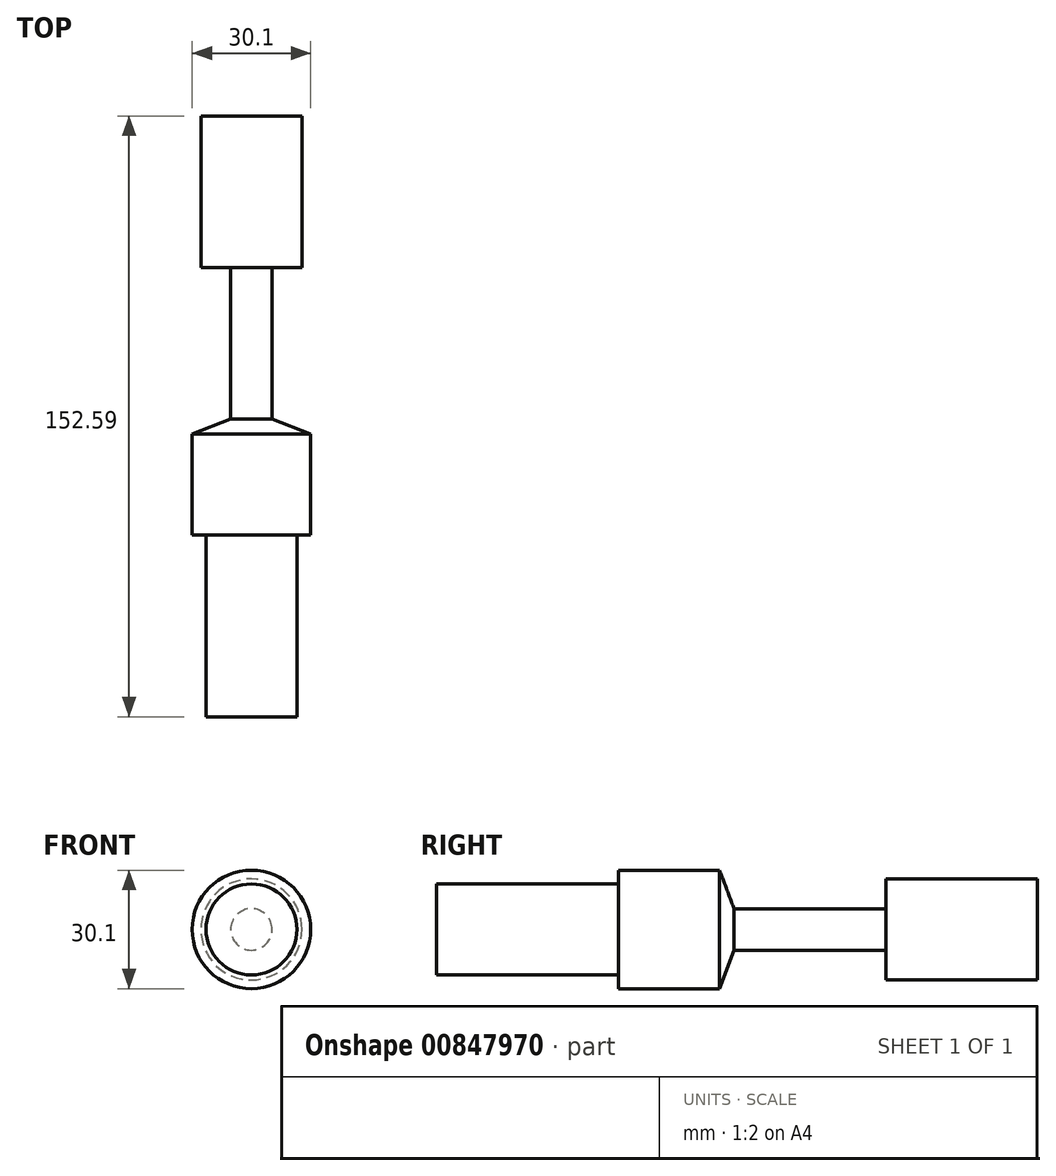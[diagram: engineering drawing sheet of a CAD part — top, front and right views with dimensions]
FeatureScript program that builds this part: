
annotation { "Feature Type Name" : "Feature", "Feature Type Description" : "" }
export const myFeature = defineFeature(function(context is Context, id is Id, definition is map)
    precondition{}
    {
        {
            var Q0;
            Q0=qCreatedBy(makeId("Top.planeOp"),FACE);
            var sketch = newSketch(context, id + "F0", { "sketchPlane" : qUnion([Q0])});
            skLineSegment(sketch, "E0", {"start": v(0, -94.32) * mm, "end": v(-11.55, -94.32) * mm});
            skLineSegment(sketch, "E1", {"start": v(-11.55, -94.32) * mm, "end": v(-11.55, -48.11) * mm});
            skLineSegment(sketch, "E2", {"start": v(-11.55, -48.11) * mm, "end": v(-15.05, -48.11) * mm});
            skLineSegment(sketch, "E3", {"start": v(-15.05, -48.11) * mm, "end": v(-15.05, -22.44) * mm});
            skLineSegment(sketch, "E4", {"start": v(-15.05, -22.44) * mm, "end": v(-5.26, -18.75) * mm});
            skLineSegment(sketch, "E5", {"start": v(-5.26, -18.75) * mm, "end": v(-5.26, 19.76) * mm});
            skLineSegment(sketch, "E6", {"start": v(-5.26, 19.76) * mm, "end": v(-12.84, 19.76) * mm});
            skLineSegment(sketch, "E7", {"start": v(-12.84, 19.76) * mm, "end": v(-12.84, 58.27) * mm});
            skLineSegment(sketch, "E8", {"start": v(-12.84, 58.27) * mm, "end": v(0, 58.27) * mm});
            skLineSegment(sketch, "E9", {"start": v(0, 58.27) * mm, "end": v(0, -94.32) * mm});
            skSolve(sketch);
        }
        {
            var Q0;
            Q0=makeQuery(id+"F0.imprint","IMPRINT",FACE,{"disambiguationData":[TD([[makeQuery(id+"F0.imprint","IMPRINT",EDGE,{"derivedFrom":sQuery(id+"F0.wireOp",EDGE,"E0")}),-1.0]])]});
            var Q1;
            Q1=sQuery(id+"F0.wireOp",EDGE,"E9");
            revolve(context, id + "F1", {"surfaceOperationType" : NewSurfaceOperationType.NEW, "entities" : qUnion([Q0]), "axis" : qUnion([Q1]), "revolveType" : RevolveType.FULL});
        }
    });
